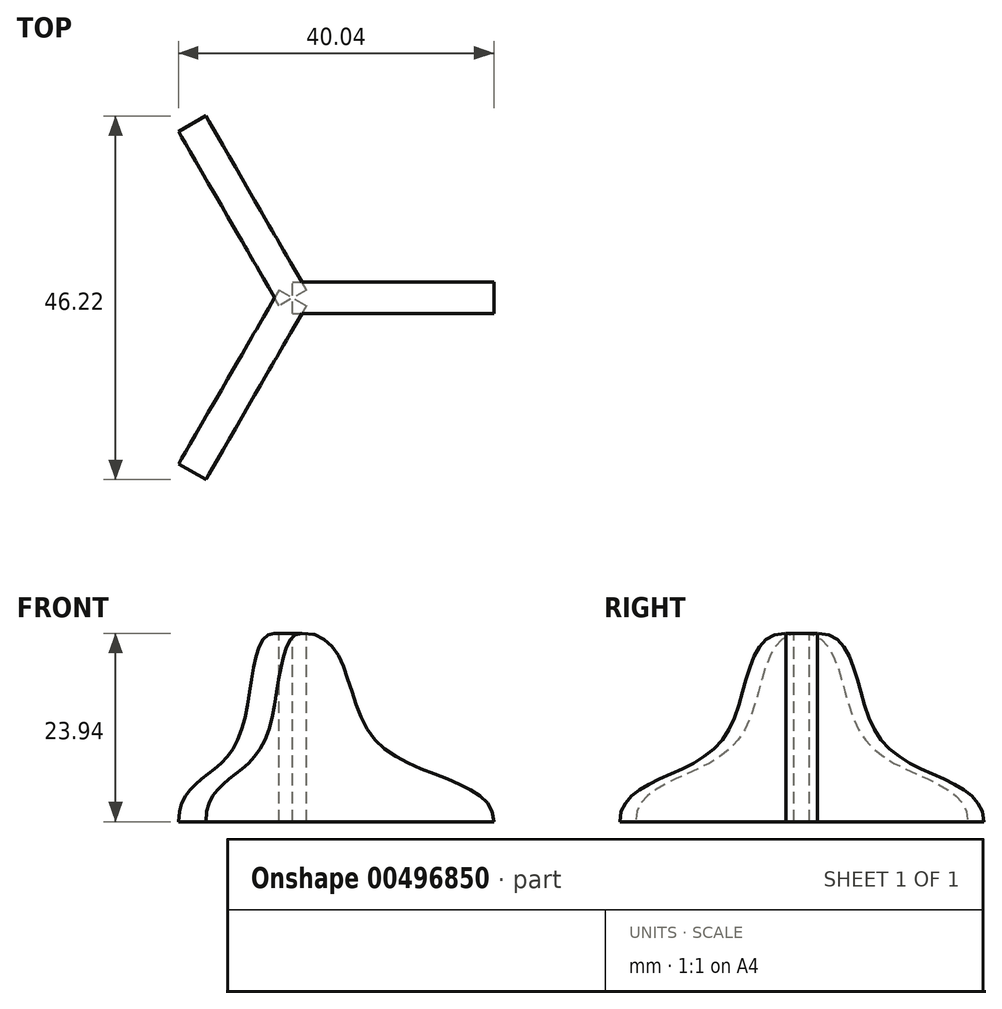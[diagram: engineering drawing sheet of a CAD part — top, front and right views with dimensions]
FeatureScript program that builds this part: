
annotation { "Feature Type Name" : "Feature", "Feature Type Description" : "" }
export const myFeature = defineFeature(function(context is Context, id is Id, definition is map)
    precondition{}
    {
        {
            var Q0;
            Q0=qCreatedBy(makeId("Front.planeOp"),FACE);
            var sketch = newSketch(context, id + "F0", { "sketchPlane" : qUnion([Q0])});
            skLineSegment(sketch, "E0", {"start": v(0, 0) * mm, "end": v(25.54, 0) * mm});
            skLineSegment(sketch, "E1", {"start": v(0, 0) * mm, "end": v(0, 23.83) * mm});
            skFitSpline(sketch, "E2", {"points": [v(0, 23.83) * mm, v(10.39, 10.48) * mm, v(25.54, 0) * mm], "startDerivative": vector(47.68, 7.55) * mm, "endDerivative": vector(0.13, -32.82) * mm});
            skSolve(sketch);
        }
        {
            var Q0;
            Q0=makeQuery(id+"F0.imprint","IMPRINT",FACE,{"disambiguationData":[TD([[makeQuery(id+"F0.imprint","IMPRINT",EDGE,{"derivedFrom":sQuery(id+"F0.wireOp",EDGE,"E0")}),1.0]])]});
            var Q1;
            Q1 = qConstructionFilter(qBodyType(qCreatedBy(id + "F0" ,EDGE), BodyType.WIRE), ConstructionObject.NO);
            extrude(context, id + "F1", {"entities" : qUnion([Q0]), "surfaceEntities" : qUnion([Q1]), "endBound" : BoundingType.SYMMETRIC, "depth" : 4 * mm});
        }
        {
            var Q0;
            Q0=qCreatedBy(makeId("Front.planeOp"),FACE);
            var sketch = newSketch(context, id + "F2", { "sketchPlane" : qUnion([Q0])});
            skLineSegment(sketch, "E3", {"start": v(0, 0) * mm, "end": v(0, 8.08) * mm});
            skSolve(sketch);
        }
        {
            var Q0;
            Q0=makeQuery(id+"F1.opExtrude","SWEPT_BODY",BODY,{"disambiguationData":[OSD([sQuery(id+"F0.wireOp",EDGE,"E0"),sQuery(id+"F0.wireOp",EDGE,"E1"),sQuery(id+"F0.wireOp",EDGE,"E2")])]});
            var Q1;
            Q1=sQuery(id+"F2.wireOp",EDGE,"E3");
            circularPattern(context, id + "F3", {"entities" : qUnion([Q0]), "axis" : qUnion([Q1]), "angle" : 360 * degree, "instanceCount" : 3, "equalSpace" : true});
        }
    });
